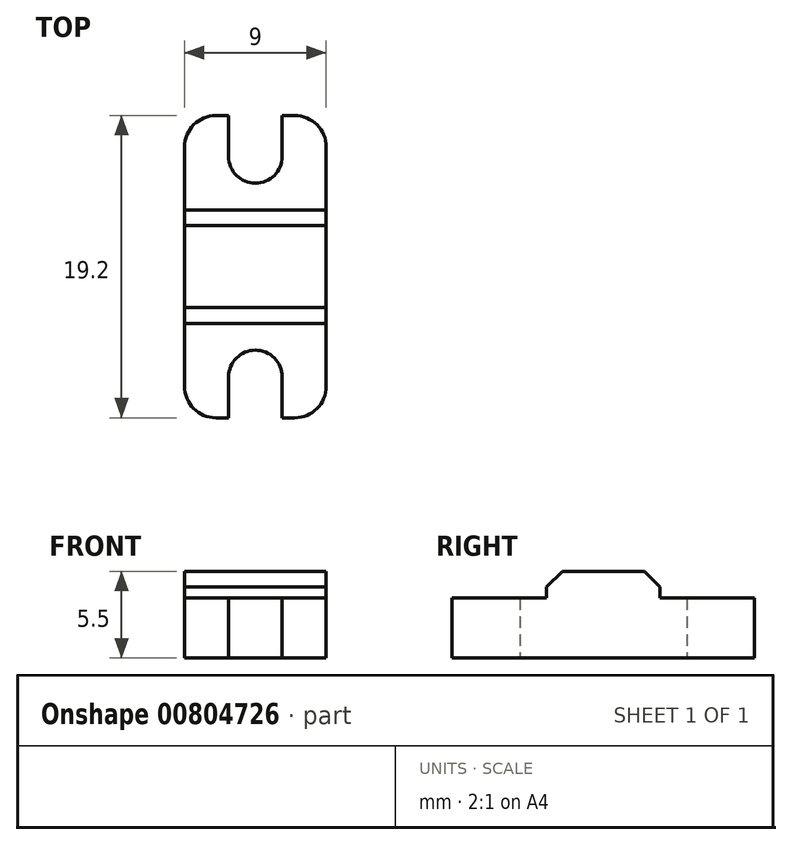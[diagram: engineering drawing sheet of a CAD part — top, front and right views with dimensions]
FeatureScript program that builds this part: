
annotation { "Feature Type Name" : "Feature", "Feature Type Description" : "" }
export const myFeature = defineFeature(function(context is Context, id is Id, definition is map)
    precondition{}
    {
        {
            var Q0;
            Q0=qCreatedBy(makeId("Top.planeOp"),FACE);
            var sketch = newSketch(context, id + "F0", { "sketchPlane" : qUnion([Q0])});
            skLineSegment(sketch, "E0", {"start": v(4.5, 0) * mm, "end": v(4.5, -7.6) * mm});
            skLineSegment(sketch, "E1", {"start": v(2.5, -9.6) * mm, "end": v(1.7, -9.6) * mm});
            skLineSegment(sketch, "E2", {"start": v(1.7, -9.6) * mm, "end": v(1.7, -7) * mm});
            skArc(sketch, "E3", {"start": v(1.7, -7) * mm, "mid": v(1.2, -5.8) * mm, "end": v(0, -5.3) * mm});
            skLineSegment(sketch, "E4", {"start": v(0, -5.3) * mm, "end": v(0, 0) * mm});
            skLineSegment(sketch, "E5", {"start": v(4.5, 0) * mm, "end": v(0, 0) * mm});
            skPoint(sketch, "E6.visualSharp", {"position": v(4.5, -9.6) * mm});
            skArc(sketch, "E6.filletArc", {"start": v(2.5, -9.6) * mm, "mid": v(3.91, -9.01) * mm, "end": v(4.5, -7.6) * mm});
            skSolve(sketch);
        }
        {
            var Q0;
            Q0=qSketchRegion(id+"F0",true);
            extrude(context, id + "F1", {"entities" : qUnion([Q0]), "depth" : 3.8 * mm, "offsetDistance" : 25 * mm});
        }
        {
            var Q0;
            Q0=makeQuery(id+"F1.opExtrude","SWEPT_FACE",FACE,{"disambiguationData":[OSD([sQuery(id+"F0.wireOp",EDGE,"E0")])]});
            var sketch = newSketch(context, id + "F2", { "sketchPlane" : qUnion([Q0])});
            skLineSegment(sketch, "E7", {"start": v(-3.6, 3.8) * mm, "end": v(-3.6, 4.5) * mm});
            skLineSegment(sketch, "E8", {"start": v(-3.6, 4.5) * mm, "end": v(-2.6, 5.5) * mm});
            skLineSegment(sketch, "E9", {"start": v(-2.6, 5.5) * mm, "end": v(0, 5.5) * mm});
            skLineSegment(sketch, "E10", {"start": v(0, 5.5) * mm, "end": v(0, 3.8) * mm});
            skLineSegment(sketch, "E11", {"start": v(0, 3.8) * mm, "end": v(-3.6, 3.8) * mm});
            skSolve(sketch);
        }
        {
            var Q0;
            Q0=qSketchRegion(id+"F2",true);
            var Q1;
            Q1=makeQuery(id+"F1.opExtrude","SWEPT_FACE",FACE,{"disambiguationData":[OSD([sQuery(id+"F0.wireOp",EDGE,"E4")])]});
            extrude(context, id + "F3", {"entities" : qUnion([Q0]), "operationType" : NewBodyOperationType.ADD, "endBound" : BoundingType.UP_TO_SURFACE, "oppositeDirection" : true, "depth" : 25 * mm, "endBoundEntityFace" : qUnion([Q1]), "offsetDistance" : 25 * mm});
        }
        {
            var Q0;
            Q0=makeQuery(id+"F1.opExtrude","SWEPT_BODY",BODY,{"disambiguationData":[OSD([sQuery(id+"F0.wireOp",EDGE,"E0"),sQuery(id+"F0.wireOp",EDGE,"E1"),sQuery(id+"F0.wireOp",EDGE,"E2"),sQuery(id+"F0.wireOp",EDGE,"E3"),sQuery(id+"F0.wireOp",EDGE,"E4"),sQuery(id+"F0.wireOp",EDGE,"E5"),sQuery(id+"F0.wireOp",EDGE,"E6.filletArc")])]});
            var Q1;
            {var subQ0=sQuery(id+"F0.wireOp",EDGE,"E4");Q1=makeQuery(id+"F3.boolean.opBoolean","MERGE",FACE,{"derivedFrom":[makeQuery(id+"F1.opExtrude","SWEPT_FACE",FACE,{"disambiguationData":[OSD([subQ0])]}),makeQuery(id+"F3.opExtrude","CAP_FACE",FACE,{"disambiguationData":[OSD([subQ0])],"isStart":false})]});}
            mirror(context, id + "F4", {"operationType" : NewBodyOperationType.ADD, "entities" : qUnion([Q0]), "mirrorPlane" : qUnion([Q1])});
        }
        {
            var Q0;
            Q0=makeQuery(id+"F1.opExtrude","SWEPT_BODY",BODY,{"disambiguationData":[OSD([sQuery(id+"F0.wireOp",EDGE,"E0"),sQuery(id+"F0.wireOp",EDGE,"E1"),sQuery(id+"F0.wireOp",EDGE,"E2"),sQuery(id+"F0.wireOp",EDGE,"E3"),sQuery(id+"F0.wireOp",EDGE,"E4"),sQuery(id+"F0.wireOp",EDGE,"E5"),sQuery(id+"F0.wireOp",EDGE,"E6.filletArc")])]});
            var Q1;
            {var subQ0=makeQuery(id+"F3.boolean.opBoolean","MERGE",FACE,{"derivedFrom":[makeQuery(id+"F1.opExtrude","SWEPT_FACE",FACE,{"disambiguationData":[OSD([sQuery(id+"F0.wireOp",EDGE,"E5")])]}),makeQuery(id+"F3.opExtrude","SWEPT_FACE",FACE,{"disambiguationData":[OSD([sQuery(id+"F2.wireOp",EDGE,"E10")])]})]});Q1=makeQuery(id+"F4.boolean.opBoolean","MERGE",FACE,{"derivedFrom":[subQ0,makeQuery(id+"F4.opPattern","COPY",FACE,{"derivedFrom":subQ0,"instanceName":"1"})]});}
            mirror(context, id + "F5", {"operationType" : NewBodyOperationType.ADD, "entities" : qUnion([Q0]), "mirrorPlane" : qUnion([Q1])});
        }
    });
